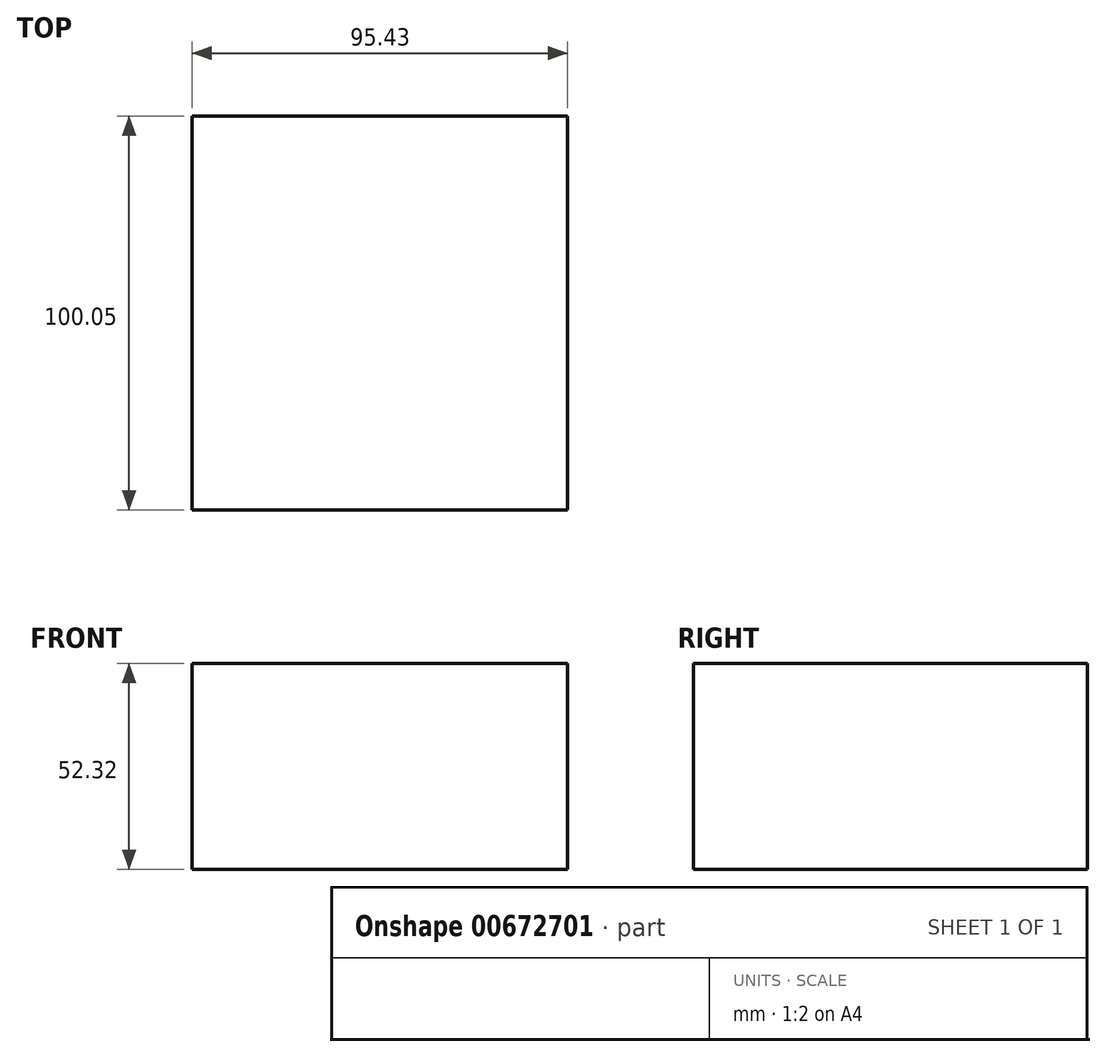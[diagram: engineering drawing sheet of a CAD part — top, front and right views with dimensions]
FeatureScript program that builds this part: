
annotation { "Feature Type Name" : "Feature", "Feature Type Description" : "" }
export const myFeature = defineFeature(function(context is Context, id is Id, definition is map)
    precondition{}
    {
        {
            var Q0;
            Q0=qCreatedBy(makeId("Top.planeOp"),FACE);
            var sketch = newSketch(context, id + "F0", { "sketchPlane" : qUnion([Q0])});
            skLineSegment(sketch, "E0.bottom", {"start": v(-38.02, -71.56) * mm, "end": v(57.4, -71.56) * mm});
            skLineSegment(sketch, "E0.top", {"start": v(-38.02, 28.5) * mm, "end": v(57.4, 28.5) * mm});
            skLineSegment(sketch, "E0.left", {"start": v(-38.02, -71.56) * mm, "end": v(-38.02, 28.5) * mm});
            skLineSegment(sketch, "E0.right", {"start": v(57.4, -71.56) * mm, "end": v(57.4, 28.5) * mm});
            skSolve(sketch);
        }
        {
            var Q0;
            Q0=makeQuery(id+"F0.imprint","IMPRINT",FACE,{"disambiguationData":[TD([[makeQuery(id+"F0.imprint","IMPRINT",EDGE,{"derivedFrom":sQuery(id+"F0.wireOp",EDGE,"E0.bottom")}),1.0]])]});
            extrude(context, id + "F1", {"entities" : qUnion([Q0]), "depth" : 52.32 * mm, "offsetDistance" : 25.4 * mm});
        }
    });
